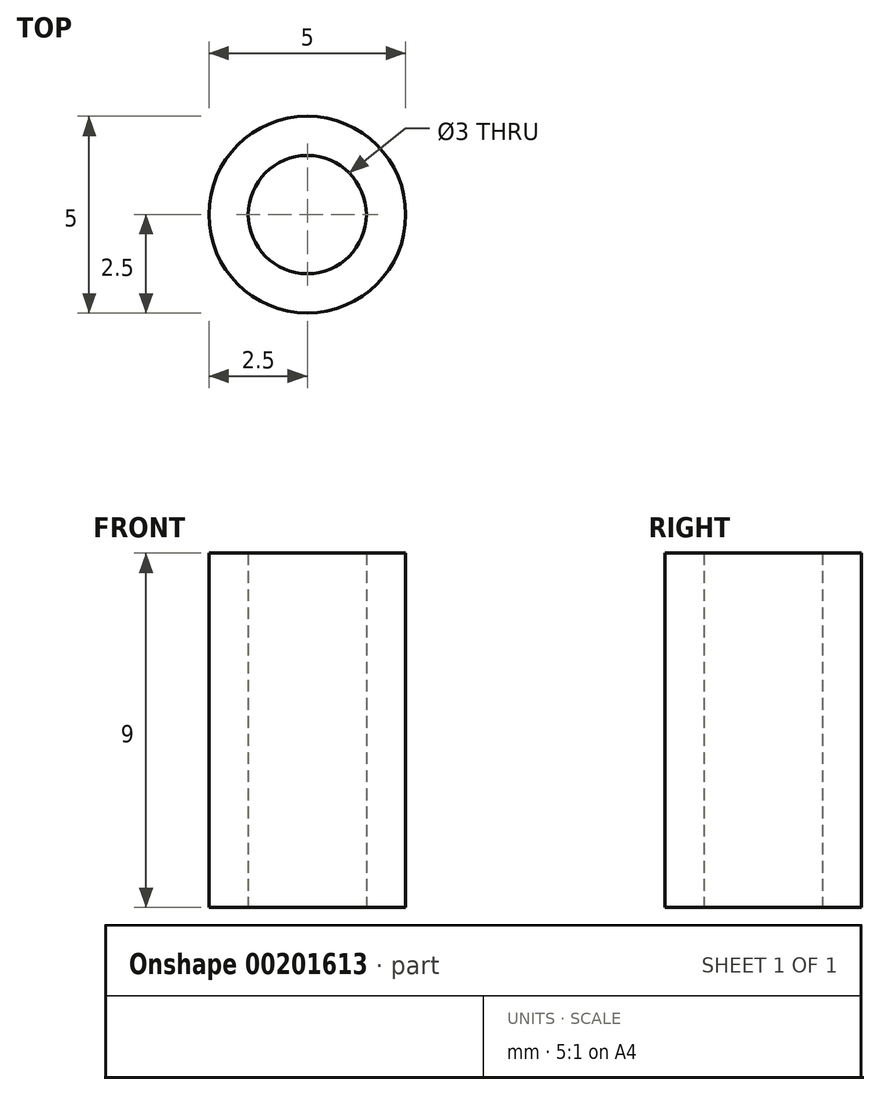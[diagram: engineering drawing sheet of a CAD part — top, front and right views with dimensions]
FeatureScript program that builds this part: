
annotation { "Feature Type Name" : "Feature", "Feature Type Description" : "" }
export const myFeature = defineFeature(function(context is Context, id is Id, definition is map)
    precondition{}
    {
        {
            var Q0;
            Q0=qCreatedBy(makeId("Top.planeOp"),FACE);
            var sketch = newSketch(context, id + "F0", { "sketchPlane" : qUnion([Q0])});
            skCircle(sketch, "E0", {"center": v(0, 0) * mm, "radius": 1.5 * mm});
            skCircle(sketch, "E1", {"center": v(0, 0) * mm, "radius": 2.5 * mm});
            skSolve(sketch);
        }
        {
            var Q0;
            Q0=makeQuery(id+"F0.imprint","IMPRINT",FACE,{"disambiguationData":[TD([[makeQuery(id+"F0.imprint","IMPRINT",EDGE,{"derivedFrom":sQuery(id+"F0.wireOp",EDGE,"E0")}),-1.0]])]});
            extrude(context, id + "F1", {"entities" : qUnion([Q0]), "depth" : 9 * mm});
        }
    });
